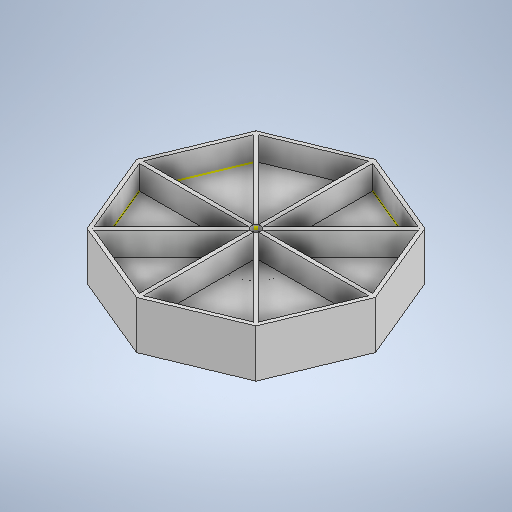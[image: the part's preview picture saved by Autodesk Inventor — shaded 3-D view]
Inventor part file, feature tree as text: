
AUTODESK INVENTOR PART (.ipt)
format: ipt  version: 2025 (Build 290162000, 162)  size: 347,136 bytes
history: native  units: mm
features: sketch x9, extrude x6, projected_geometry x2
ambient origin geometry x8: Origin, YZ Plane, XZ Plane, XY Plane, X Axis, Y Axis, Z Axis, Center Point
bodies: Body1 (feature_tree)
feature tree (17):
  extrude  "Wyciągnięcie proste2"  Depth=300.0mm
  sketch  "Szkic4"
  extrude  "Wyciągnięcie proste3"  Depth=50.0mm TaperAngle=0.0deg
  sketch  "Szkic6"
  extrude  "Wyciągnięcie proste4"  Depth=290.0mm
  extrude  "Wyciągnięcie proste5"  Depth=30.0mm TaperAngle=0.0deg
  extrude  "Wyciągnięcie proste6"  Depth=5.0mm
  sketch  "Szkic10"
  extrude  "Wyciągnięcie proste7"  Depth=5.0mm
  sketch  "Szkic3"
  sketch  "Szkic5"
  sketch  "Szkic7"
  sketch  "Szkic8"
  sketch  "Szkic9"
  sketch  "Szkic11"
  projected_geometry  "Pętla rzutowana1"
  projected_geometry  "Pętla rzutowana2"
